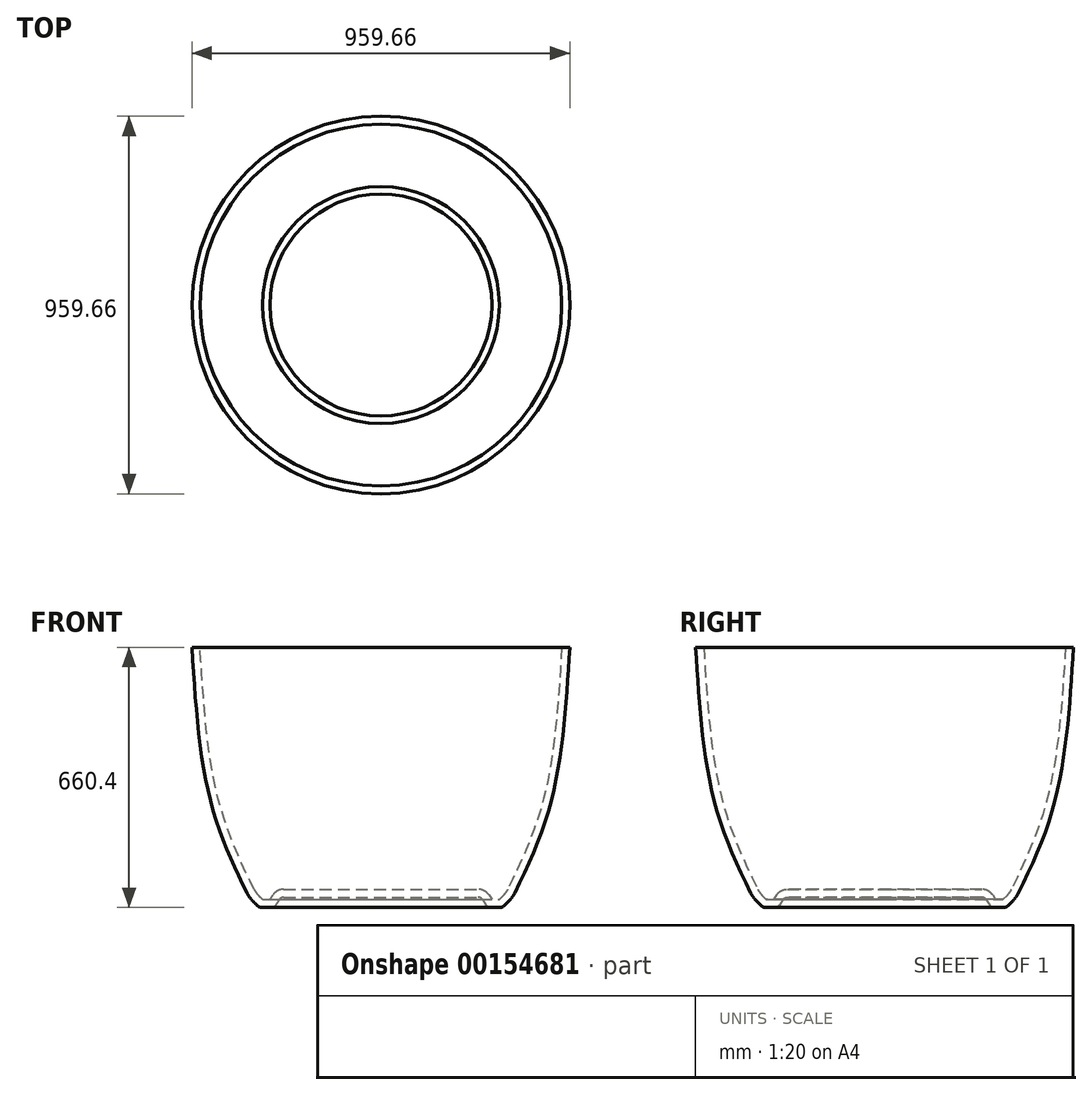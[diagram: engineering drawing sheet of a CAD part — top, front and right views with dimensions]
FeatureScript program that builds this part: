
annotation { "Feature Type Name" : "Feature", "Feature Type Description" : "" }
export const myFeature = defineFeature(function(context is Context, id is Id, definition is map)
    precondition{}
    {
        {
            var Q0;
            Q0=qCreatedBy(makeId("Front.planeOp"),FACE);
            var sketch = newSketch(context, id + "F0", { "sketchPlane" : qUnion([Q0])});
            skLineSegment(sketch, "E0", {"start": v(0, 0) * mm, "end": v(247.27, 0) * mm});
            skLineSegment(sketch, "E1", {"start": v(257.78, -5.56) * mm, "end": v(267.48, -19.84) * mm});
            skPoint(sketch, "E2.visualSharp", {"position": v(254, 0) * mm});
            skArc(sketch, "E2.filletArc", {"start": v(257.78, -5.56) * mm, "mid": v(253.22, -1.48) * mm, "end": v(247.27, 0) * mm});
            skLineSegment(sketch, "E3", {"start": v(277.98, -25.4) * mm, "end": v(304.09, -25.4) * mm});
            skLineSegment(sketch, "E4", {"start": v(313.08, -21.67) * mm, "end": v(325.81, -8.92) * mm});
            skPoint(sketch, "E5.visualSharp", {"position": v(271.25, -25.4) * mm});
            skArc(sketch, "E5.filletArc", {"start": v(267.48, -19.84) * mm, "mid": v(272.04, -23.92) * mm, "end": v(277.98, -25.4) * mm});
            skPoint(sketch, "E6.visualSharp", {"position": v(309.35, -25.4) * mm});
            skArc(sketch, "E6.filletArc", {"start": v(304.09, -25.4) * mm, "mid": v(308.95, -24.43) * mm, "end": v(313.08, -21.67) * mm});
            skLineSegment(sketch, "E7", {"start": v(0, 0) * mm, "end": v(0, 635) * mm});
            skFitSpline(sketch, "E8", {"points": [v(334.72, 0) * mm, v(434.35, 250.63) * mm, v(479.83, 635) * mm], "startDerivative": vector(253.66, 515.29) * mm, "endDerivative": vector(45.72, 747.77) * mm});
            skLineSegment(sketch, "E9", {"start": v(0, 635) * mm, "end": v(479.83, 635) * mm});
            skArc(sketch, "E10.filletArc", {"start": v(325.81, -8.92) * mm, "mid": v(333.9, 0.63) * mm, "end": v(340.32, 11.38) * mm});
            skSolve(sketch);
        }
        {
            var Q0;
            Q0=makeQuery(id+"F0.imprint","IMPRINT",FACE,{"disambiguationData":[TD([[makeQuery(id+"F0.imprint","IMPRINT",EDGE,{"derivedFrom":sQuery(id+"F0.wireOp",EDGE,"E0")}),1.0]])]});
            var Q1;
            Q1=sQuery(id+"F0.wireOp",EDGE,"E7");
            revolve(context, id + "F1", {"entities" : qUnion([Q0]), "axis" : qUnion([Q1]), "revolveType" : RevolveType.FULL});
        }
        {
            var Q0;
            Q0=makeQuery(id+"F1.opRevolve","SWEPT_FACE",FACE,{"disambiguationData":[OSD([sQuery(id+"F0.wireOp",EDGE,"E9")])]});
            shell(context, id + "F2", {"entities" : qUnion([Q0]), "thickness" : 20.32 * mm});
        }
        {
            var Q0;
            Q0=qCreatedBy(makeId("Front.planeOp"),FACE);
            var sketch = newSketch(context, id + "F3", { "sketchPlane" : qUnion([Q0])});
            skFitSpline(sketch, "E11", {"points": [v(472.54, 608.73) * mm, v(731.02, 489.12) * mm, v(643.36, 152.46) * mm, v(335.8, 35.5) * mm], "startDerivative": vector(533.88, -206.2) * mm, "endDerivative": vector(-988.05, -186.22) * mm});
            skSolve(sketch);
        }
        {
            var Q0;
            Q0=qCreatedBy(makeId("Right.planeOp"),FACE);
            var Q1;
            Q1=sQuery(id+"F3.wireOp",VERTEX,"E11.0.internal");
            cPlane(context, id + "F4", {"entities" : qUnion([Q0, Q1]), "cplaneType" : CPlaneType.PLANE_POINT, "offset" : 25.4 * mm, "width" : 152.4 * mm, "height" : 152.4 * mm});
        }
        {
            var Q0;
            Q0=qCreatedBy(id+"F4.planeOp",FACE);
            var sketch = newSketch(context, id + "F5", { "sketchPlane" : qUnion([Q0])});
            skEllipse(sketch, "E12", {"center": v(0, 609.7) * mm, "majorRadius": 31.78 * mm, "minorRadius": 13.21 * mm, "majorAxis": v(-1, 0)});
            skSolve(sketch);
        }
    });
